# Revit family: 926-01-002 DN100-1600
name_source: partatom
category: Pipe Accessories
units: mm (PartAtom-declared; Revit-internal decimal feet)

## family parameters
Always vertical = Yes
Cut with Voids When Loaded = No
Part Type = Valve - Breaks Into
Round Connector Dimension = Use Diameter
Shared = No
Work Plane-Based = No

## types (15) — shared parameters
DN1000_PN25 = 926-A10-01-030060100000
DN100_PN25 = 926-100-01-030160100000
DN1200_PN25 = 926-A12-01-030060100000
DN150_PN25 = 926-150-01-030080100000
DN1600_PN25 = 926-A16-01-030060100000
DN200_PN25 = 926-200-01-030080100000
DN250 PN25 = 926-250-01-030080100000
DN300_PN25 = 926-300-01-030080100000
DN350_PN25 = 926-350-01-030080100000
DN400_PN25 = 926-400-01-030080100000
DN500_PN25 = 926-500-01-030080100000
DN600_PN25 = 926-600-01-030080100000
DN700_PN25 = 926-700-01-030060100000
DN800_PN25 = 926-800-01-030060100000
DN900_PN25 = 926-900-01-030060100000
Description_ = AVK DBL. ECC. BUTTERFLY VALVE, FLANGED, ISO5752/13, PN25
Search_table = 926-01-002 DN100-1600
URL_product_pages = https://www.avkvalves.com
zero-valued in all types: Default Elevation

## per-type parameters (varying)
- DN100_PN25: A=127 mm; A_support=80 mm; A_support1=38 mm  [stored 0.124672 ft]; Actuator_FL_T=19 mm  [stored 0.062336 ft]; Actuator_Flange_R=63 mm; B=130 mm; Base_R=45 mm; Base_T=20 mm  [stored 0.0656168 ft]; Body_Thickness=6 mm  [stored 0.019685 ft]; Body_rib=8 mm  [stored 0.0262467 ft]; Body_shaft_R=25 mm  [stored 0.082021 ft]; Body_void=18 mm  [stored 0.0590551 ft]; Bore_R=50 mm; C=202 mm; D=11 mm  [stored 0.0360892 ft]; D1=15 mm; DN=100 mm; E=20 mm  [stored 0.0656168 ft]; Flange_R=95 mm; Flange_T=19 mm  [stored 0.062336 ft]; PCD=90 mm; Raised_R=77 mm; Raised_dis=3 mm  [stored 0.00984252 ft]; Slot_Location1=20 mm  [stored 0.0656168 ft]; Stem_dim1=8 mm  [stored 0.0262467 ft]; stem1=15 mm; support_t=8 mm  [stored 0.0262467 ft]
- DN1000_PN25: A=410 mm; A_support=195 mm; A_support1=105 mm; Actuator_FL_T=35 mm  [stored 0.114829 ft]; Actuator_Flange_R=175 mm; B=700 mm; Base_R=140 mm; Base_T=46 mm; Body_Thickness=12 mm  [stored 0.0393701 ft]; Body_rib=25 mm  [stored 0.082021 ft]; Body_shaft_R=82 mm; Body_void=57 mm; Bore_R=500 mm; C=856 mm; D=75 mm; D1=49 mm; DN=1000 mm; E=80 mm; Flange_R=615 mm; Flange_T=35 mm  [stored 0.114829 ft]; PCD=580 mm; Raised_R=556 mm; Raised_dis=5 mm  [stored 0.0164042 ft]; Slot_Location1=53 mm; Stem_dim1=20 mm  [stored 0.0656168 ft]; stem1=49 mm; support_t=12 mm  [stored 0.0393701 ft]
- DN1200_PN25: A=470 mm; A_support=235 mm; A_support1=125 mm; Actuator_FL_T=40 mm  [stored 0.131234 ft]; Actuator_Flange_R=208 mm; B=850 mm; Base_R=166 mm; Base_T=52 mm; Body_Thickness=12 mm  [stored 0.0393701 ft]; Body_rib=25 mm  [stored 0.082021 ft]; Body_shaft_R=94 mm; Body_void=66 mm; Bore_R=600 mm; C=1080 mm; D=143 mm; D1=56 mm; DN=1200 mm; E=180 mm; Flange_R=728 mm; Flange_T=40 mm  [stored 0.131234 ft]; PCD=690 mm; Raised_R=665 mm; Raised_dis=5 mm  [stored 0.0164042 ft]; Slot_Location1=65 mm; Stem_dim1=25 mm  [stored 0.082021 ft]; stem1=56 mm; support_t=12 mm  [stored 0.0393701 ft]
- DN200_PN25: A=152 mm; A_support=112 mm; A_support1=45 mm; Actuator_FL_T=19 mm  [stored 0.062336 ft]; Actuator_Flange_R=75 mm; B=200 mm; Base_R=60 mm; Base_T=25 mm  [stored 0.082021 ft]; Body_Thickness=7 mm  [stored 0.0229659 ft]; Body_rib=8 mm  [stored 0.0262467 ft]; Body_shaft_R=30 mm  [stored 0.0984252 ft]; Body_void=21 mm; Bore_R=100 mm; C=320 mm; D=22 mm  [stored 0.0721785 ft]; D1=18 mm  [stored 0.0590551 ft]; DN=200 mm; E=30 mm  [stored 0.0984252 ft]; Flange_R=150 mm; Flange_T=19 mm  [stored 0.062336 ft]; PCD=148 mm; Raised_R=132 mm; Raised_dis=3 mm  [stored 0.00984252 ft]; Slot_Location1=31 mm  [stored 0.101706 ft]; Stem_dim1=12 mm  [stored 0.0393701 ft]; stem1=18 mm  [stored 0.0590551 ft]; support_t=8 mm  [stored 0.0262467 ft]
- DN150_PN25: A=140 mm; A_support=96 mm; A_support1=38 mm  [stored 0.124672 ft]; Actuator_FL_T=19 mm  [stored 0.062336 ft]; Actuator_Flange_R=63 mm; B=170 mm; Base_R=50 mm; Base_T=23 mm  [stored 0.0754593 ft]; Body_Thickness=6 mm  [stored 0.019685 ft]; Body_rib=8 mm  [stored 0.0262467 ft]; Body_shaft_R=28 mm  [stored 0.0918635 ft]; Body_void=20 mm  [stored 0.0656168 ft]; Bore_R=75 mm; C=280 mm; D=17 mm  [stored 0.0557743 ft]; D1=17 mm  [stored 0.0557743 ft]; DN=150 mm; E=27 mm  [stored 0.0885827 ft]; Flange_R=122 mm; Flange_T=19 mm  [stored 0.062336 ft]; PCD=120 mm; Raised_R=105 mm; Raised_dis=3 mm  [stored 0.00984252 ft]; Slot_Location1=26 mm; Stem_dim1=10 mm  [stored 0.0328084 ft]; stem1=17 mm  [stored 0.0557743 ft]; support_t=8 mm  [stored 0.0262467 ft]
- DN1600_PN25: A=600 mm; A_support=166 mm; A_support1=143 mm; Actuator_FL_T=40 mm  [stored 0.131234 ft]; Actuator_Flange_R=238 mm; B=1050 mm; Base_R=190 mm; Base_T=52 mm; Body_Thickness=1 mm  [stored 0.00328084 ft]; Body_rib=25 mm  [stored 0.082021 ft]; Body_shaft_R=120 mm; Body_void=84 mm; Bore_R=800 mm; C=1050 mm; D=180 mm; D1=72 mm; DN=1600 mm; E=170 mm; Flange_R=830 mm; Flange_T=40 mm  [stored 0.131234 ft]; PCD=715 mm; Raised_R=815 mm; Raised_dis=5 mm  [stored 0.0164042 ft]; Slot_Location1=42 mm; Stem_dim1=16 mm  [stored 0.0524934 ft]; stem1=71 mm; support_t=12 mm  [stored 0.0393701 ft]
- DN250 PN25: A=165 mm; A_support=115 mm; A_support1=45 mm; Actuator_FL_T=22 mm  [stored 0.0721785 ft]; Actuator_Flange_R=75 mm; B=222 mm; Base_R=60 mm; Base_T=29 mm; Body_Thickness=8 mm  [stored 0.0262467 ft]; Body_rib=8 mm  [stored 0.0262467 ft]; Body_shaft_R=33 mm  [stored 0.108268 ft]; Body_void=23 mm  [stored 0.0754593 ft]; Bore_R=125 mm; C=340 mm; D=27 mm  [stored 0.0885827 ft]; D1=20 mm  [stored 0.0656168 ft]; DN=250 mm; E=36 mm  [stored 0.11811 ft]; Flange_R=175 mm; Flange_T=22 mm  [stored 0.0721785 ft]; PCD=175 mm; Raised_R=160 mm; Raised_dis=3 mm  [stored 0.00984252 ft]; Slot_Location1=31 mm  [stored 0.101706 ft]; Stem_dim1=12 mm  [stored 0.0393701 ft]; stem1=20 mm  [stored 0.0656168 ft]; support_t=8 mm  [stored 0.0262467 ft]
- DN300_PN25: A=178 mm; A_support=105 mm; A_support1=45 mm; Actuator_FL_T=25 mm  [stored 0.082021 ft]; Actuator_Flange_R=75 mm; B=260 mm; Base_R=60 mm; Base_T=32 mm; Body_Thickness=8 mm  [stored 0.0262467 ft]; Body_rib=13 mm; Body_shaft_R=36 mm  [stored 0.11811 ft]; Body_void=25 mm  [stored 0.082021 ft]; Bore_R=150 mm; C=390 mm; D=27 mm  [stored 0.0885827 ft]; D1=21 mm; DN=300 mm; E=41 mm  [stored 0.134514 ft]; Flange_R=215 mm; Flange_T=25 mm  [stored 0.082021 ft]; PCD=200 mm; Raised_R=184 mm; Raised_dis=4 mm  [stored 0.0131234 ft]; Slot_Location1=27 mm  [stored 0.0885827 ft]; Stem_dim1=10 mm  [stored 0.0328084 ft]; stem1=21 mm; support_t=8 mm  [stored 0.0262467 ft]
- DN350_PN25: A=190 mm; A_support=115 mm; A_support1=45 mm; Actuator_FL_T=25 mm  [stored 0.082021 ft]; Actuator_Flange_R=75 mm; B=290 mm; Base_R=60 mm; Base_T=32 mm; Body_Thickness=9 mm  [stored 0.0295276 ft]; Body_rib=13 mm; Body_shaft_R=38 mm  [stored 0.124672 ft]; Body_void=27 mm  [stored 0.0885827 ft]; Bore_R=175 mm; C=420 mm; D=36 mm  [stored 0.11811 ft]; D1=23 mm  [stored 0.0754593 ft]; DN=350 mm; E=41 mm  [stored 0.134514 ft]; Flange_R=253 mm; Flange_T=25 mm  [stored 0.082021 ft]; PCD=230 mm; Raised_R=214 mm; Raised_dis=4 mm  [stored 0.0131234 ft]; Slot_Location1=30 mm  [stored 0.0984252 ft]; Stem_dim1=11 mm  [stored 0.0360892 ft]; stem1=23 mm  [stored 0.0754593 ft]; support_t=9 mm  [stored 0.0295276 ft]
- DN400_PN25: A=216 mm; A_support=140 mm; A_support1=63 mm; Actuator_FL_T=25 mm  [stored 0.082021 ft]; Actuator_Flange_R=105 mm; B=350 mm; Base_R=84 mm; Base_T=32 mm; Body_Thickness=9 mm  [stored 0.0295276 ft]; Body_rib=16 mm  [stored 0.0524934 ft]; Body_shaft_R=43 mm; Body_void=30 mm  [stored 0.0984252 ft]; Bore_R=200 mm; C=451 mm; D=36 mm  [stored 0.11811 ft]; D1=26 mm; DN=400 mm; E=41 mm  [stored 0.134514 ft]; Flange_R=283 mm; Flange_T=25 mm  [stored 0.082021 ft]; PCD=258 mm; Raised_R=239 mm; Raised_dis=4 mm  [stored 0.0131234 ft]; Slot_Location1=39 mm  [stored 0.127953 ft]; Stem_dim1=15 mm; stem1=26 mm; support_t=9 mm  [stored 0.0295276 ft]
- DN500_PN25: A=229 mm; A_support=140 mm; A_support1=63 mm; Actuator_FL_T=27 mm  [stored 0.0885827 ft]; Actuator_Flange_R=105 mm; B=380 mm; Base_R=84 mm; Base_T=34 mm; Body_Thickness=10 mm  [stored 0.0328084 ft]; Body_rib=16 mm  [stored 0.0524934 ft]; Body_shaft_R=46 mm; Body_void=32 mm; Bore_R=250 mm; C=511 mm; D=46 mm; D1=27 mm  [stored 0.0885827 ft]; DN=500 mm; E=65 mm; Flange_R=335 mm; Flange_T=27 mm  [stored 0.0885827 ft]; PCD=310 mm; Raised_R=291 mm; Raised_dis=4 mm  [stored 0.0131234 ft]; Slot_Location1=38 mm  [stored 0.124672 ft]; Stem_dim1=14 mm  [stored 0.0459318 ft]; stem1=27 mm  [stored 0.0885827 ft]; support_t=10 mm  [stored 0.0328084 ft]
- DN600_PN25: A=267 mm; A_support=160 mm; A_support1=90 mm; Actuator_FL_T=30 mm  [stored 0.0984252 ft]; Actuator_Flange_R=150 mm; B=450 mm; Base_R=120 mm; Base_T=39 mm  [stored 0.127953 ft]; Body_Thickness=10 mm  [stored 0.0328084 ft]; Body_rib=16 mm  [stored 0.0524934 ft]; Body_shaft_R=53 mm; Body_void=37 mm; Bore_R=300 mm; C=561 mm; D=55 mm; D1=32 mm; DN=600 mm; E=70 mm; Flange_R=380 mm; Flange_T=30 mm  [stored 0.0984252 ft]; PCD=363 mm; Raised_R=341 mm; Raised_dis=5 mm  [stored 0.0164042 ft]; Slot_Location1=43 mm; Stem_dim1=16 mm  [stored 0.0524934 ft]; stem1=32 mm; support_t=10 mm  [stored 0.0328084 ft]
- DN700_PN25: A=292 mm; A_support=180 mm; A_support1=90 mm; Actuator_FL_T=33 mm  [stored 0.108268 ft]; Actuator_Flange_R=150 mm; B=500 mm; Base_R=120 mm; Base_T=42 mm; Body_Thickness=10 mm  [stored 0.0328084 ft]; Body_rib=18 mm  [stored 0.0590551 ft]; Body_shaft_R=58 mm; Body_void=41 mm  [stored 0.134514 ft]; Bore_R=350 mm; C=655 mm; D=80 mm; D1=35 mm  [stored 0.114829 ft]; DN=700 mm; E=110 mm; Flange_R=440 mm; Flange_T=33 mm  [stored 0.108268 ft]; PCD=420 mm; Raised_R=399 mm; Raised_dis=5 mm  [stored 0.0164042 ft]; Slot_Location1=49 mm; Stem_dim1=19 mm  [stored 0.062336 ft]; stem1=35 mm  [stored 0.114829 ft]; support_t=10 mm  [stored 0.0328084 ft]
- DN800_PN25: A=318 mm; A_support=205 mm; A_support1=90 mm; Actuator_FL_T=35 mm  [stored 0.114829 ft]; Actuator_Flange_R=150 mm; B=600 mm; Base_R=120 mm; Base_T=46 mm; Body_Thickness=10 mm  [stored 0.0328084 ft]; Body_rib=20 mm  [stored 0.0656168 ft]; Body_shaft_R=64 mm; Body_void=45 mm; Bore_R=400 mm; C=740 mm; D=80 mm; D1=38 mm  [stored 0.124672 ft]; DN=800 mm; E=110 mm; Flange_R=508 mm; Flange_T=35 mm  [stored 0.114829 ft]; PCD=475 mm; Raised_R=452 mm; Raised_dis=5 mm  [stored 0.0164042 ft]; Slot_Location1=57 mm; Stem_dim1=22 mm  [stored 0.0721785 ft]; stem1=38 mm  [stored 0.124672 ft]; support_t=10 mm  [stored 0.0328084 ft]
- DN900_PN25: A=330 mm; A_support=210 mm; A_support1=105 mm; Actuator_FL_T=38 mm  [stored 0.124672 ft]; Actuator_Flange_R=175 mm; B=620 mm; Base_R=140 mm; Base_T=49 mm; Body_Thickness=11 mm  [stored 0.0360892 ft]; Body_rib=25 mm  [stored 0.082021 ft]; Body_shaft_R=66 mm; Body_void=46 mm; Bore_R=450 mm; C=802 mm; D=75 mm; D1=40 mm  [stored 0.131234 ft]; DN=900 mm; E=108 mm; Flange_R=550 mm; Flange_T=38 mm  [stored 0.124672 ft]; PCD=525 mm; Raised_R=502 mm; Raised_dis=5 mm  [stored 0.0164042 ft]; Slot_Location1=58 mm; Stem_dim1=22 mm  [stored 0.0721785 ft]; stem1=39 mm  [stored 0.127953 ft]; support_t=12 mm  [stored 0.0393701 ft]

note: [stored X ft] marks values corroborated as IEEE doubles in the binary element streams (Revit-internal decimal feet)

## geometry (parser evidence)
native form markers: Sweep x4
no freeform markers — native parametric forms only
